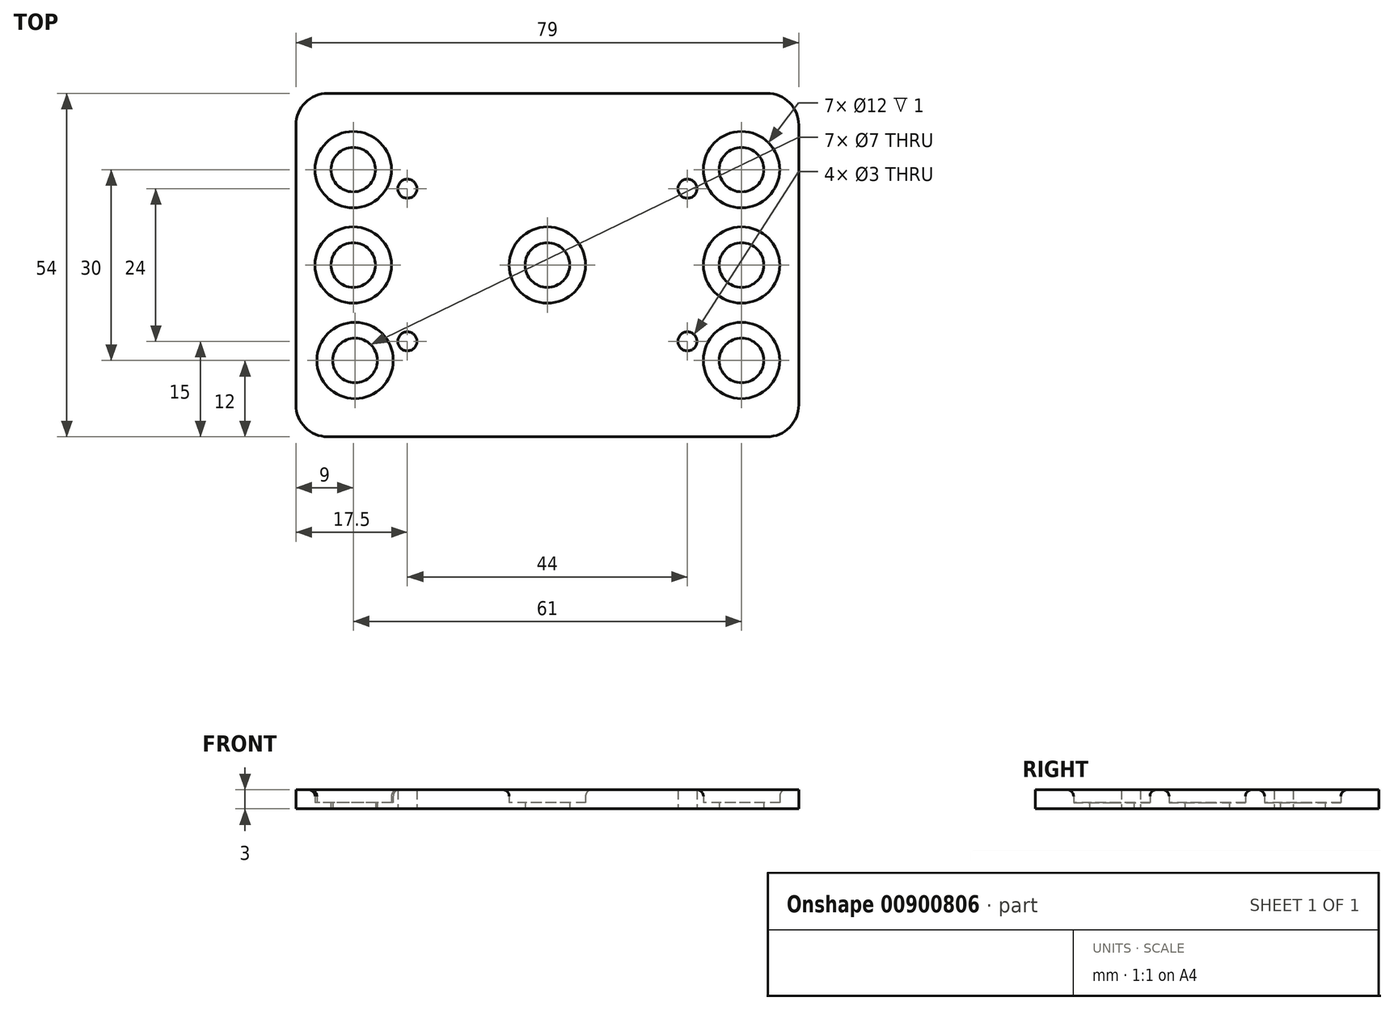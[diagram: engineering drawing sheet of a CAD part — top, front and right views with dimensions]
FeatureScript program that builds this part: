
annotation { "Feature Type Name" : "Feature", "Feature Type Description" : "" }
export const myFeature = defineFeature(function(context is Context, id is Id, definition is map)
    precondition{}
    {
        {
            var Q0;
            Q0=qCreatedBy(makeId("Top.planeOp"),FACE);
            var sketch = newSketch(context, id + "F0", { "sketchPlane" : qUnion([Q0])});
            skCircle(sketch, "E0", {"center": v(30.5, 15) * mm, "radius": 3.5 * mm});
            skCircle(sketch, "E1", {"center": v(30.5, 0) * mm, "radius": 3.5 * mm});
            skCircle(sketch, "E2", {"center": v(-30.5, 15) * mm, "radius": 3.5 * mm});
            skCircle(sketch, "E3", {"center": v(-30.5, 0) * mm, "radius": 3.5 * mm});
            skCircle(sketch, "E4", {"center": v(-30.21, -15) * mm, "radius": 3.5 * mm});
            skCircle(sketch, "E5", {"center": v(30.5, -15) * mm, "radius": 3.5 * mm});
            skCircle(sketch, "E6", {"center": v(-30.5, 15) * mm, "radius": 6 * mm});
            skCircle(sketch, "E7", {"center": v(30.5, 15) * mm, "radius": 6 * mm});
            skCircle(sketch, "E8", {"center": v(30.5, 0) * mm, "radius": 6 * mm});
            skCircle(sketch, "E9", {"center": v(30.5, -15) * mm, "radius": 6 * mm});
            skCircle(sketch, "E10", {"center": v(-30.21, -15) * mm, "radius": 6 * mm});
            skCircle(sketch, "E11", {"center": v(-30.5, 0) * mm, "radius": 6 * mm});
            skLineSegment(sketch, "E12.bottom", {"start": v(39.5, -27) * mm, "end": v(-39.5, -27) * mm});
            skLineSegment(sketch, "E12.top", {"start": v(39.5, 27) * mm, "end": v(-39.5, 27) * mm});
            skLineSegment(sketch, "E12.left", {"start": v(39.5, -27) * mm, "end": v(39.5, 27) * mm});
            skLineSegment(sketch, "E12.right", {"start": v(-39.5, -27) * mm, "end": v(-39.5, 27) * mm});
            skPoint(sketch, "E12.middle", {"position": v(0, 0) * mm});
            skCircle(sketch, "E13", {"center": v(0, 0) * mm, "radius": 3.5 * mm});
            skCircle(sketch, "E14", {"center": v(0, 0) * mm, "radius": 6 * mm});
            skCircle(sketch, "E15", {"center": v(-22, 12) * mm, "radius": 1.5 * mm});
            skCircle(sketch, "E16", {"center": v(22, 12) * mm, "radius": 1.5 * mm});
            skCircle(sketch, "E17", {"center": v(22, -12) * mm, "radius": 1.5 * mm});
            skCircle(sketch, "E18", {"center": v(-22, -12) * mm, "radius": 1.5 * mm});
            skSolve(sketch);
        }
        {
            var Q0;
            Q0=makeQuery(id+"F0.imprint","IMPRINT",FACE,{"disambiguationData":[TD([[makeQuery(id+"F0.imprint","IMPRINT",EDGE,{"derivedFrom":sQuery(id+"F0.wireOp",EDGE,"E6")}),-1.0]])]});
            extrude(context, id + "F1", {"entities" : qUnion([Q0]), "depth" : 3 * mm, "offsetDistance" : 25 * mm});
        }
        {
            var Q0;
            Q0=makeQuery(id+"F0.imprint","IMPRINT",FACE,{"disambiguationData":[TD([[makeQuery(id+"F0.imprint","IMPRINT",EDGE,{"derivedFrom":sQuery(id+"F0.wireOp",EDGE,"E2")}),-1.0]])]});
            var Q1;
            Q1=makeQuery(id+"F0.imprint","IMPRINT",FACE,{"disambiguationData":[TD([[makeQuery(id+"F0.imprint","IMPRINT",EDGE,{"derivedFrom":sQuery(id+"F0.wireOp",EDGE,"E0")}),-1.0]])]});
            var Q2;
            Q2=makeQuery(id+"F0.imprint","IMPRINT",FACE,{"disambiguationData":[TD([[makeQuery(id+"F0.imprint","IMPRINT",EDGE,{"derivedFrom":sQuery(id+"F0.wireOp",EDGE,"E1")}),-1.0]])]});
            var Q3;
            Q3=makeQuery(id+"F0.imprint","IMPRINT",FACE,{"disambiguationData":[TD([[makeQuery(id+"F0.imprint","IMPRINT",EDGE,{"derivedFrom":sQuery(id+"F0.wireOp",EDGE,"E5")}),-1.0]])]});
            var Q4;
            Q4=makeQuery(id+"F0.imprint","IMPRINT",FACE,{"disambiguationData":[TD([[makeQuery(id+"F0.imprint","IMPRINT",EDGE,{"derivedFrom":sQuery(id+"F0.wireOp",EDGE,"E4")}),-1.0]])]});
            var Q5;
            Q5=makeQuery(id+"F0.imprint","IMPRINT",FACE,{"disambiguationData":[TD([[makeQuery(id+"F0.imprint","IMPRINT",EDGE,{"derivedFrom":sQuery(id+"F0.wireOp",EDGE,"E3")}),-1.0]])]});
            var Q6;
            Q6=makeQuery(id+"F0.imprint","IMPRINT",FACE,{"disambiguationData":[TD([[makeQuery(id+"F0.imprint","IMPRINT",EDGE,{"derivedFrom":sQuery(id+"F0.wireOp",EDGE,"E13")}),-1.0]])]});
            extrude(context, id + "F2", {"entities" : qUnion([Q0, Q1, Q2, Q3, Q4, Q5, Q6]), "operationType" : NewBodyOperationType.ADD, "depth" : 1 * mm, "offsetDistance" : 25 * mm});
        }
        {
            var Q0;
            Q0=makeQuery(id+"F1.opExtrude","CAP_EDGE",EDGE,{"disambiguationData":[OSD([sQuery(id+"F0.wireOp",EDGE,"E6")])],"isStart":false});
            var Q1;
            Q1=makeQuery(id+"F1.opExtrude","CAP_EDGE",EDGE,{"disambiguationData":[OSD([sQuery(id+"F0.wireOp",EDGE,"E7")])],"isStart":false});
            var Q2;
            Q2=makeQuery(id+"F1.opExtrude","CAP_EDGE",EDGE,{"disambiguationData":[OSD([sQuery(id+"F0.wireOp",EDGE,"E8")])],"isStart":false});
            var Q3;
            Q3=makeQuery(id+"F1.opExtrude","CAP_EDGE",EDGE,{"disambiguationData":[OSD([sQuery(id+"F0.wireOp",EDGE,"E9")])],"isStart":false});
            var Q4;
            Q4=makeQuery(id+"F1.opExtrude","CAP_EDGE",EDGE,{"disambiguationData":[OSD([sQuery(id+"F0.wireOp",EDGE,"E10")])],"isStart":false});
            var Q5;
            Q5=makeQuery(id+"F1.opExtrude","CAP_EDGE",EDGE,{"disambiguationData":[OSD([sQuery(id+"F0.wireOp",EDGE,"E11")])],"isStart":false});
            var Q6;
            Q6=makeQuery(id+"F1.opExtrude","CAP_EDGE",EDGE,{"disambiguationData":[OSD([sQuery(id+"F0.wireOp",EDGE,"E14")])],"isStart":false});
            fillet(context, id + "F3", {"entities" : qUnion([Q0, Q1, Q2, Q3, Q4, Q5, Q6]), "radius" : 1 * mm, "tangentPropagation" : true, "allowEdgeOverflow" : false});
        }
        {
            var Q0;
            Q0=makeQuery(id+"F1.opExtrude","SWEPT_EDGE",EDGE,{"disambiguationData":[OSD([sQuery(id+"F0.wireOp",EDGE,"E12.bottom"),sQuery(id+"F0.wireOp",EDGE,"E12.right")])]});
            var Q1;
            Q1=makeQuery(id+"F1.opExtrude","SWEPT_EDGE",EDGE,{"disambiguationData":[OSD([sQuery(id+"F0.wireOp",EDGE,"E12.bottom"),sQuery(id+"F0.wireOp",EDGE,"E12.left")])]});
            var Q2;
            Q2=makeQuery(id+"F1.opExtrude","SWEPT_EDGE",EDGE,{"disambiguationData":[OSD([sQuery(id+"F0.wireOp",EDGE,"E12.top"),sQuery(id+"F0.wireOp",EDGE,"E12.left")])]});
            var Q3;
            Q3=makeQuery(id+"F1.opExtrude","SWEPT_EDGE",EDGE,{"disambiguationData":[OSD([sQuery(id+"F0.wireOp",EDGE,"E12.top"),sQuery(id+"F0.wireOp",EDGE,"E12.right")])]});
            fillet(context, id + "F4", {"entities" : qUnion([Q0, Q1, Q2, Q3]), "radius" : 5 * mm, "tangentPropagation" : true, "allowEdgeOverflow" : false});
        }
    });
